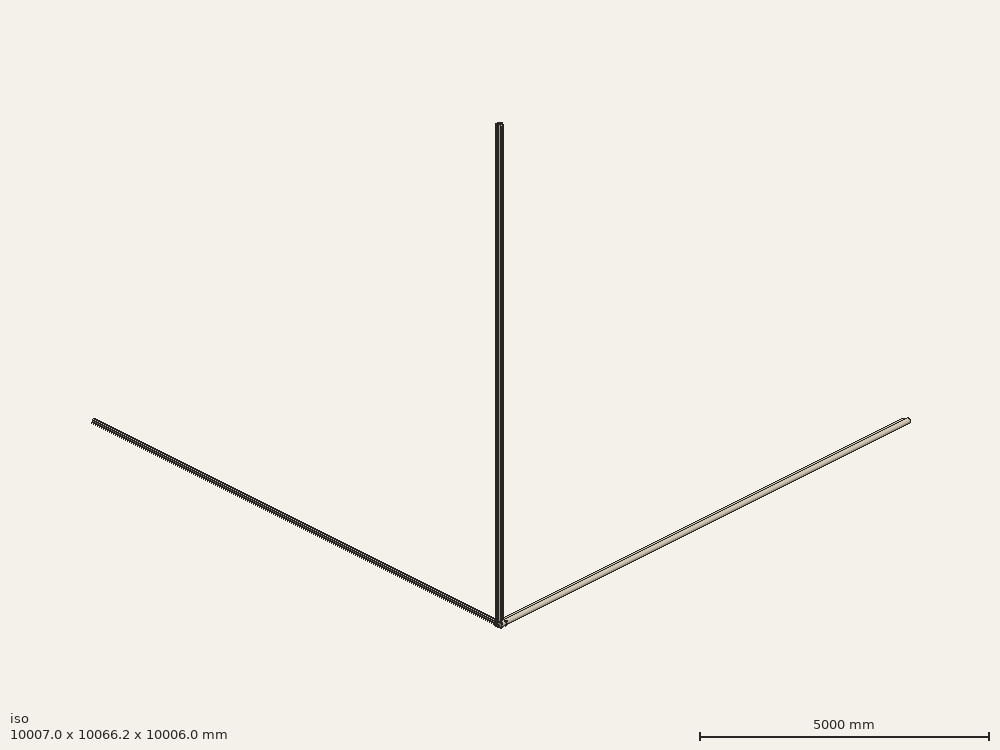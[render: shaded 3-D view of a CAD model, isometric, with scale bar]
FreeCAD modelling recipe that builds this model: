
FCSTD DOCUMENT  (FreeCAD 0.16R6705 (Git))
Label: Hip3
License: All rights reserved
LicenseURL: http://en.wikipedia.org/wiki/All_rights_reserved
objects: PartDesign::Fillet×48, PartDesign::Chamfer×22, Sketcher::SketchObject×16, PartDesign::Pocket×15, PartDesign::PolarPattern×3, PartDesign::Pad×1
note: 121 computed .brp shape members not serialized (recipe doc carries the construction recipe); baked Part::Feature solids carry a one-line shape summary decoded from their .brp

FEATURE [Sketcher::SketchObject] Sketch
  sketch-geometry (29):
    g0: Circle [constr] CenterX=0 CenterY=0 CenterZ=0 NormalX=0 NormalY=0 NormalZ=1 Radius=40
    g1: LineSegment [constr] StartX=-39 StartY=-40 StartZ=0 EndX=-25 EndY=-40 EndZ=0
    g2: LineSegment [constr] StartX=-25 StartY=-40 StartZ=0 EndX=-25 EndY=-120 EndZ=0
    g3: LineSegment [constr] StartX=-25 StartY=-120 StartZ=0 EndX=-39 EndY=-120 EndZ=0
    g4: LineSegment [constr] StartX=-39 StartY=-120 StartZ=0 EndX=-39 EndY=-30 EndZ=0
    g5: LineSegment [constr] StartX=25 StartY=-40 StartZ=0 EndX=39 EndY=-40 EndZ=0
    g6: LineSegment [constr] StartX=39 StartY=-40 StartZ=0 EndX=39 EndY=-120 EndZ=0
    g7: LineSegment [constr] StartX=39 StartY=-120 StartZ=0 EndX=25 EndY=-120 EndZ=0
    g8: LineSegment [constr] StartX=25 StartY=-120 StartZ=0 EndX=25 EndY=-40 EndZ=0
    g9: LineSegment [constr] StartX=-25 StartY=-120 StartZ=0 EndX=25 EndY=-120 EndZ=0
    g10: LineSegment [constr] StartX=-39 StartY=-80 StartZ=0 EndX=39 EndY=-80 EndZ=0
    g11: LineSegment [constr] StartX=-39 StartY=65 StartZ=0 EndX=61 EndY=65 EndZ=0
    g12: LineSegment [constr] StartX=39 StartY=-65 StartZ=0 EndX=-39 EndY=-65 EndZ=0
    g13: GeomPoint [constr] X=0 Y=-80 Z=0
    g14: LineSegment StartX=-68 StartY=44 StartZ=0 EndX=68 EndY=44 EndZ=0
    g15: LineSegment StartX=68 StartY=44 StartZ=0 EndX=68 EndY=-65 EndZ=0
    g16: LineSegment StartX=68 StartY=-65 StartZ=0 EndX=-68 EndY=-65 EndZ=0
    g17: LineSegment StartX=-68 StartY=-65 StartZ=0 EndX=-68 EndY=44 EndZ=0
    g18: LineSegment [constr] StartX=-39 StartY=-30 StartZ=0 EndX=-68 EndY=-30 EndZ=0
    g19: LineSegment [constr] StartX=-68 StartY=-30 StartZ=0 EndX=-68 EndY=-130 EndZ=0
    g20: LineSegment [constr] StartX=-68 StartY=-130 StartZ=0 EndX=-39 EndY=-130 EndZ=0
    g21: LineSegment [constr] StartX=-39 StartY=-130 StartZ=0 EndX=-39 EndY=-120 EndZ=0
    g22: Circle CenterX=0 CenterY=0 CenterZ=0 NormalX=0 NormalY=0 NormalZ=1 Radius=18
    g23: Circle [constr] CenterX=0 CenterY=0 CenterZ=0 NormalX=0 NormalY=0 NormalZ=1 Radius=51
    g24: Circle CenterX=-47 CenterY=-50 CenterZ=0 NormalX=0 NormalY=0 NormalZ=1 Radius=1.7
    g25: Circle CenterX=-47 CenterY=-60 CenterZ=0 NormalX=0 NormalY=0 NormalZ=1 Radius=1.7
    g26: Circle CenterX=47 CenterY=-50 CenterZ=0 NormalX=0 NormalY=0 NormalZ=1 Radius=1.7
    g27: Circle CenterX=47 CenterY=-60 CenterZ=0 NormalX=0 NormalY=0 NormalZ=1 Radius=1.7
    g28: LineSegment [constr] StartX=-47 StartY=-50 StartZ=0 EndX=-47 EndY=-60 EndZ=0
  constraints (81):
    c: Radius(g0) = 40
    c: Coincident(g2,g3)
    c: Coincident(g3,g4)
    c: Horizontal(g3)
    c: Vertical(g2)
    c: Vertical(g4)
    c: Coincident(g5,g6)
    c: Coincident(g6,g7)
    c: Coincident(g7,g8)
    c: Horizontal(g7)
    c: Vertical(g6)
    c: Vertical(g8)
    c: Coincident(g9,g2)
    c: Coincident(g9,g7)
    c: Horizontal(g9)
    c: DistanceX(g1,g5) = 50
    c: DistanceY(g6,g5) = 80
    c: DistanceX(g1,g1) = 14
    c: PointOnObject(g10,g4)
    c: Horizontal(g10)
    c: Symmetric(g5,g6,g10)
    c: Horizontal(g11)
    c: Horizontal(g12)
    c: Symmetric(g12,g11,g-1)
    c: DistanceX(g11,g11) = 100
    c: DistanceY(g10,g12) = 15
    c: Symmetric(g3,g5,g13)
    c: DistanceY(g13,g-1) = 80
    c: Coincident(g0,g-1)
    c: Coincident(g14,g15)
    c: Coincident(g15,g16)
    c: Coincident(g16,g17)
    c: Coincident(g17,g14)
    c: Horizontal(g16)
    c: Vertical(g15)
    c: Vertical(g17)
    c: DistanceX(g14,g14) = 136
    c: DistanceX(g16,g12) = 29
    c: PointOnObject(g12,g16)
    c: Horizontal(g18)
    c: Coincident(g18,g19)
    c: Vertical(g19)
    c: Coincident(g19,g20)
    c: Horizontal(g20)
    c: Coincident(g20,g21)
    c: Coincident(g21,g3)
    c: Vertical(g21)
    c: Symmetric(g18,g20,g10)
    c: DistanceY(g19,g18) = 100
    c: DistanceX(g19,g20) = 29
    c: Horizontal(g14)
    c: Symmetric(g14,g14,g-2)
    c: DistanceY(g16,g14) = 109
    c: Coincident(g22,g-1)
    c: Radius(g22) = 18
    c: Horizontal(g5)
    c: Horizontal(g1)
    c: Symmetric(g5,g1,g-2)
    c: Coincident(g4,g18)
    c: PointOnObject(g1,g4)
    c: PointOnObject(g12,g4)
    c: Coincident(g23,g-1)
    c: Radius(g23) = 51
    c: Coincident(g2,g1)
    c: Coincident(g5,g8)
    c: Symmetric(g5,g1,g-2)
    c: DistanceY(g12,g-1) = 65
    c: Symmetric(g12,g12,g-2)
    c: DistanceY(g-1,g14) = 44
    c: DistanceY(g24,g4) = 20
    c: DistanceY(g25,g24) = 10
    c: Symmetric(g24,g26,g-2)
    c: Symmetric(g25,g27,g-2)
    c: Radius(g27) = 1.7
    c: Equal(g27,g26)
    c: Equal(g27,g24)
    c: Equal(g27,g25)
    c: Coincident(g28,g24)
    c: Coincident(g28,g25)
    c: Vertical(g28)
    c: DistanceX(g24,g1) = 8
FEATURE [PartDesign::Pad] Pad
  Length = 44
  Length2 = 100
  Sketch = -> Sketch
  Type = 0
FEATURE [Sketcher::SketchObject] Sketch001  label="SideCut"
  Placement = pos=(-68,0,0) rot=(0.57735,-0.57735,-0.57735;2.0944rad)
  Support = -> Pad [Face4]
  sketch-geometry (29):
    g0: Circle CenterX=80 CenterY=58 CenterZ=0 NormalX=0 NormalY=0 NormalZ=1 Radius=51.2
    g1: LineSegment [constr] StartX=-50 StartY=-14 StartZ=0 EndX=50 EndY=-14 EndZ=0
    g2: LineSegment [constr] StartX=50 StartY=-14 StartZ=0 EndX=50 EndY=-43 EndZ=0
    g3: LineSegment [constr] StartX=50 StartY=-43 StartZ=0 EndX=-50 EndY=-43 EndZ=0
    g4: LineSegment [constr] StartX=-50 StartY=-43 StartZ=0 EndX=-50 EndY=-14 EndZ=0
    g5: LineSegment [constr] StartX=-40 StartY=0 StartZ=0 EndX=40 EndY=0 EndZ=0
    g6: LineSegment [constr] StartX=40 StartY=0 StartZ=0 EndX=40 EndY=-14 EndZ=0
    g7: LineSegment [constr] StartX=40 StartY=-14 StartZ=0 EndX=-40 EndY=-14 EndZ=0
    g8: LineSegment [constr] StartX=-40 StartY=-14 StartZ=0 EndX=-40 EndY=0 EndZ=0
    g9: LineSegment [constr] StartX=30 StartY=108 StartZ=0 EndX=130 EndY=108 EndZ=0
    g10: LineSegment [constr] StartX=130 StartY=108 StartZ=0 EndX=130 EndY=8 EndZ=0
    g11: LineSegment [constr] StartX=130 StartY=8 StartZ=0 EndX=30 EndY=8 EndZ=0
    g12: LineSegment [constr] StartX=30 StartY=8 StartZ=0 EndX=30 EndY=108 EndZ=0
    g13: LineSegment StartX=22 StartY=50 StartZ=0 EndX=22 EndY=44 EndZ=0
    g14: LineSegment StartX=-8 StartY=14 StartZ=0 EndX=-28 EndY=14 EndZ=0
    g15: LineSegment StartX=-28 StartY=20 StartZ=0 EndX=-50 EndY=20 EndZ=0
    g16: LineSegment StartX=-50 StartY=20 StartZ=0 EndX=-50 EndY=50 EndZ=0
    g17: LineSegment StartX=-50 StartY=50 StartZ=0 EndX=22 EndY=50 EndZ=0
    g18: GeomPoint [constr] X=0 Y=14 Z=0
    g19: LineSegment StartX=32.75 StartY=17.25 StartZ=0 EndX=39.25 EndY=17.25 EndZ=0
    g20: LineSegment StartX=39.25 StartY=17.25 StartZ=0 EndX=39.25 EndY=10.75 EndZ=0
    g21: LineSegment StartX=39.25 StartY=10.75 StartZ=0 EndX=32.75 EndY=10.75 EndZ=0
    g22: LineSegment StartX=32.75 StartY=10.75 StartZ=0 EndX=32.75 EndY=17.25 EndZ=0
    g23: GeomPoint [constr] X=36 Y=14 Z=0
    g24: LineSegment StartX=-28 StartY=20 StartZ=0 EndX=-28 EndY=14 EndZ=0
    g25: Circle CenterX=36 CenterY=23 CenterZ=0 NormalX=0 NormalY=0 NormalZ=1 Radius=1.7
    g26: LineSegment [constr] StartX=36 StartY=23 StartZ=0 EndX=36 EndY=14 EndZ=0
    g27: Circle CenterX=-40 CenterY=14 CenterZ=0 NormalX=0 NormalY=0 NormalZ=1 Radius=1.5
    g28: ArcOfCircle CenterX=-8 CenterY=44 CenterZ=0 NormalX=0 NormalY=0 NormalZ=1 Radius=30 StartAngle=4.71239 EndAngle=6.28319
  constraints (82):
    c: DistanceX(g-1,g0) = 80
    c: Radius(g0) = 51.2
    c: DistanceY(g-1,g0) = 58
    c: Coincident(g1,g2)
    c: Coincident(g2,g3)
    c: Coincident(g3,g4)
    c: Coincident(g4,g1)
    c: Horizontal(g1)
    c: Horizontal(g3)
    c: Vertical(g2)
    c: Vertical(g4)
    c: Symmetric(g1,g1,g-2)
    c: DistanceX(g3,g2) = 100
    c: DistanceY(g3,g1) = 29
    c: DistanceY(g1,g-1) = 14
    c: Coincident(g5,g6)
    c: Coincident(g6,g7)
    c: Coincident(g7,g8)
    c: Coincident(g8,g5)
    c: Horizontal(g5)
    c: Horizontal(g7)
    c: Vertical(g6)
    c: Vertical(g8)
    c: Symmetric(g5,g5,g-2)
    c: DistanceY(g7,g5) = 14
    c: PointOnObject(g-1,g5)
    c: DistanceX(g7,g6) = 80
    c: Coincident(g9,g10)
    c: Coincident(g10,g11)
    c: Coincident(g11,g12)
    c: Coincident(g12,g9)
    c: Horizontal(g9)
    c: Horizontal(g11)
    c: Vertical(g10)
    c: Vertical(g12)
    c: Equal(g10,g9)
    c: Symmetric(g11,g9,g0)
    c: DistanceY(g10,g9) = 100
    c: Vertical(g13)
    c: Horizontal(g14)
    c: Horizontal(g15)
    c: Coincident(g15,g16)
    c: Vertical(g16)
    c: Coincident(g16,g17)
    c: Coincident(g17,g13)
    c: Horizontal(g17)
    c: DistanceX(g13,g9) = 8
    c: DistanceY(g-1,g16) = 50
    c: DistanceX(g16,g-1) = 50
    c: PointOnObject(g18,g14)
    c: PointOnObject(g18,g-2)
    c: DistanceY(g-1,g18) = 14
    c: DistanceX(g-1,g11) = 30
    c: Coincident(g19,g20)
    c: Coincident(g20,g21)
    c: Coincident(g21,g22)
    c: Coincident(g22,g19)
    c: Horizontal(g19)
    c: Horizontal(g21)
    c: Vertical(g20)
    c: Vertical(g22)
    c: Equal(g20,g19)
    c: Symmetric(g20,g19,g23)
    c: DistanceY(g11,g23) = 6
    c: DistanceX(g11,g23) = 6
    c: DistanceY(g20,g19) = 6.5
    c: Coincident(g24,g15)
    c: Vertical(g24)
    c: Coincident(g14,g24)
    c: Radius(g25) = 1.7
    c: DistanceY(g23,g25) = 9
    c: DistanceY(g11,g15) = 12
    c: DistanceX(g15,g18) = 28
    c: Coincident(g26,g25)
    c: Coincident(g26,g23)
    c: Vertical(g26)
    c: DistanceX(g27,g18) = 40
    c: Radius(g27) = 1.5
    c: DistanceY(g27,g15) = 6
    c: Tangent(g13,g28) = 1.5708
    c: Tangent(g14,g28) = 1.5708
    c: DistanceY(g14,g13) = 30
FEATURE [PartDesign::Pocket] Pocket
  Length = 5
  Sketch = -> Sketch001
  Type = 1
FEATURE [Sketcher::SketchObject] Sketch002  label="UpCut"
  Placement = pos=(0,-65,0) rot=(1,0,0;1.5708rad)
  Support = -> Pocket [Face6]
  sketch-geometry (30):
    g0: LineSegment StartX=-25 StartY=50 StartZ=0 EndX=25 EndY=50 EndZ=0
    g1: LineSegment StartX=25 StartY=50 StartZ=0 EndX=25 EndY=14 EndZ=0
    g2: LineSegment StartX=25 StartY=14 StartZ=0 EndX=-25 EndY=14 EndZ=0
    g3: LineSegment StartX=-25 StartY=14 StartZ=0 EndX=-25 EndY=50 EndZ=0
    g4: LineSegment StartX=-65.25 StartY=17.25 StartZ=0 EndX=-58.75 EndY=17.25 EndZ=0
    g5: LineSegment StartX=-58.75 StartY=17.25 StartZ=0 EndX=-58.75 EndY=10.75 EndZ=0
    g6: LineSegment StartX=-58.75 StartY=10.75 StartZ=0 EndX=-65.25 EndY=10.75 EndZ=0
    g7: LineSegment StartX=-65.25 StartY=10.75 StartZ=0 EndX=-65.25 EndY=17.25 EndZ=0
    g8: LineSegment StartX=58.75 StartY=17.25 StartZ=0 EndX=65.25 EndY=17.25 EndZ=0
    g9: LineSegment StartX=65.25 StartY=17.25 StartZ=0 EndX=65.25 EndY=10.75 EndZ=0
    g10: LineSegment StartX=65.25 StartY=10.75 StartZ=0 EndX=58.75 EndY=10.75 EndZ=0
    g11: LineSegment StartX=58.75 StartY=10.75 StartZ=0 EndX=58.75 EndY=17.25 EndZ=0
    g12: GeomPoint [constr] X=62 Y=14 Z=0
    g13: GeomPoint [constr] X=-62 Y=14 Z=0
    g14: Circle CenterX=-47 CenterY=38 CenterZ=0 NormalX=0 NormalY=0 NormalZ=1 Radius=1.7
    g15: Circle CenterX=-47 CenterY=28 CenterZ=0 NormalX=0 NormalY=0 NormalZ=1 Radius=1.7
    g16: Circle CenterX=47 CenterY=38 CenterZ=0 NormalX=0 NormalY=0 NormalZ=1 Radius=1.7
    g17: Circle CenterX=47 CenterY=28 CenterZ=0 NormalX=0 NormalY=0 NormalZ=1 Radius=1.7
    g18: LineSegment [constr] StartX=-68 StartY=108 StartZ=0 EndX=-39 EndY=108 EndZ=0
    g19: LineSegment [constr] StartX=-39 StartY=108 StartZ=0 EndX=-39 EndY=8 EndZ=0
    g20: LineSegment [constr] StartX=-39 StartY=8 StartZ=0 EndX=-68 EndY=8 EndZ=0
    g21: LineSegment [constr] StartX=-68 StartY=8 StartZ=0 EndX=-68 EndY=108 EndZ=0
    g22: LineSegment [constr] StartX=39 StartY=108 StartZ=0 EndX=68 EndY=108 EndZ=0
    g23: LineSegment [constr] StartX=68 StartY=108 StartZ=0 EndX=68 EndY=8 EndZ=0
    g24: LineSegment [constr] StartX=68 StartY=8 StartZ=0 EndX=39 EndY=8 EndZ=0
    g25: LineSegment [constr] StartX=39 StartY=8 StartZ=0 EndX=39 EndY=108 EndZ=0
    g26: LineSegment [constr] StartX=-47 StartY=38 StartZ=0 EndX=-47 EndY=28 EndZ=0
    g27: LineSegment [constr] StartX=47 StartY=38 StartZ=0 EndX=47 EndY=28 EndZ=0
    g28: LineSegment [constr] StartX=-68 StartY=58 StartZ=0 EndX=-39 EndY=58 EndZ=0
    g29: LineSegment [constr] StartX=-39 StartY=8 StartZ=0 EndX=39 EndY=8 EndZ=0
  constraints (87):
    c: Coincident(g0,g1)
    c: Coincident(g3,g0)
    c: Horizontal(g0)
    c: Horizontal(g2)
    c: Vertical(g1)
    c: Vertical(g3)
    c: Symmetric(g0,g0,g-2)
    c: Symmetric(g2,g2,g-2)
    c: DistanceY(g-1,g2) = 14
    c: DistanceY(g-1,g0) = 50
    c: DistanceX(g0,g0) = 50
    c: Coincident(g4,g5)
    c: Coincident(g5,g6)
    c: Coincident(g6,g7)
    c: Coincident(g7,g4)
    c: Horizontal(g4)
    c: Horizontal(g6)
    c: Vertical(g5)
    c: Vertical(g7)
    c: Coincident(g8,g9)
    c: Coincident(g9,g10)
    c: Coincident(g10,g11)
    c: Coincident(g11,g8)
    c: Horizontal(g8)
    c: Horizontal(g10)
    c: Vertical(g9)
    c: Vertical(g11)
    c: Equal(g9,g8)
    c: Equal(g8,g4)
    c: Equal(g4,g7)
    c: DistanceY(g9,g8) = 6.5
    c: Symmetric(g6,g4,g13)
    c: Symmetric(g8,g10,g12)
    c: Symmetric(g12,g13,g-2)
    c: DistanceX(g13,g3) = 37
    c: Coincident(g2,g1)
    c: Coincident(g2,g3)
    c: Radius(g15) = 1.7
    c: Equal(g15,g14)
    c: Equal(g15,g16)
    c: Equal(g15,g17)
    c: Coincident(g18,g19)
    c: Coincident(g19,g20)
    c: Coincident(g20,g21)
    c: Coincident(g21,g18)
    c: Horizontal(g18)
    c: Horizontal(g20)
    c: Vertical(g19)
    c: Vertical(g21)
    c: Coincident(g22,g23)
    c: Coincident(g23,g24)
    c: Coincident(g24,g25)
    c: Coincident(g25,g22)
    c: Horizontal(g22)
    c: Horizontal(g24)
    c: Vertical(g23)
    c: Vertical(g25)
    c: DistanceX(g18,g18) = 29
    c: DistanceY(g20,g18) = 100
    c: DistanceX(g19,g2) = 14
    c: DistanceX(g1,g24) = 14
    c: Symmetric(g18,g22,g-2)
    c: Symmetric(g22,g18,g-2)
    c: Coincident(g26,g14)
    c: Coincident(g26,g15)
    c: Coincident(g27,g16)
    c: Coincident(g27,g17)
    c: Vertical(g27)
    c: DistanceY(g26,g26) = 10
    c: DistanceY(g27,g27) = 10
    c: Symmetric(g14,g16,g-2)
    c: Vertical(g26)
    c: DistanceX(g20,g15) = 21
    c: PointOnObject(g28,g21)
    c: Horizontal(g28)
    c: PointOnObject(g28,g19)
    c: Symmetric(g18,g20,g28)
    c: DistanceY(g14,g28) = 20
    c: Coincident(g29,g19)
    c: Coincident(g29,g24)
    c: Horizontal(g29)
    c: DistanceY(g20,g13) = 6
    c: DistanceY(g19,g15) = 20
    c: DistanceX(g15,g19) = 8
    c: DistanceX(g14,g16) = 94
    c: DistanceY(g-1,g14) = 38
    c: DistanceY(g-1,g20) = 8
FEATURE [PartDesign::Pocket] Pocket001
  Length = 5
  Sketch = -> Sketch002
  Type = 1
FEATURE [Sketcher::SketchObject] Sketch003  label="FixedRingCutout1"
  Placement = pos=(-68,0,0) rot=(0.57735,-0.57735,-0.57735;2.0944rad)
  Support = -> Pocket001 [Face9]
  sketch-geometry (4):
    g0: LineSegment StartX=30 StartY=108 StartZ=0 EndX=130 EndY=108 EndZ=0
    g1: LineSegment StartX=130 StartY=108 StartZ=0 EndX=130 EndY=8 EndZ=0
    g2: LineSegment StartX=130 StartY=8 StartZ=0 EndX=30 EndY=8 EndZ=0
    g3: LineSegment StartX=30 StartY=8 StartZ=0 EndX=30 EndY=108 EndZ=0
  constraints (12):
    c: Coincident(g0,g1)
    c: Coincident(g1,g2)
    c: Coincident(g2,g3)
    c: Coincident(g3,g0)
    c: Horizontal(g0)
    c: Horizontal(g2)
    c: Vertical(g1)
    c: Vertical(g3)
    c: DistanceY(g-1,g2) = 8
    c: DistanceX(g-1,g2) = 30
    c: DistanceY(g1,g0) = 100
    c: DistanceX(g2,g1) = 100
FEATURE [PartDesign::Pocket] Pocket002
  Length = 29
  Sketch = -> Sketch003
  Type = 0
FEATURE [Sketcher::SketchObject] Sketch004  label="FixedRingCutout2"
  Placement = pos=(68,0,0) rot=(0.57735,0.57735,0.57735;2.0944rad)
  Support = -> Pocket002 [Face3]
  sketch-geometry (4):
    g0: LineSegment StartX=-130 StartY=108 StartZ=0 EndX=-30 EndY=108 EndZ=0
    g1: LineSegment StartX=-30 StartY=108 StartZ=0 EndX=-30 EndY=8 EndZ=0
    g2: LineSegment StartX=-30 StartY=8 StartZ=0 EndX=-130 EndY=8 EndZ=0
    g3: LineSegment StartX=-130 StartY=8 StartZ=0 EndX=-130 EndY=108 EndZ=0
  constraints (12):
    c: Coincident(g0,g1)
    c: Coincident(g1,g2)
    c: Coincident(g2,g3)
    c: Coincident(g3,g0)
    c: Horizontal(g0)
    c: Horizontal(g2)
    c: Vertical(g1)
    c: Vertical(g3)
    c: Equal(g0,g3)
    c: DistanceY(g2,g0) = 100
    c: DistanceY(g-1,g1) = 8
    c: DistanceX(g1,g-1) = 30
FEATURE [PartDesign::Pocket] Pocket003
  Length = 29
  Sketch = -> Sketch004
  Type = 0
FEATURE [Sketcher::SketchObject] Sketch007  label="InnerRing"
  Placement = pos=(0,0,14) rot=(0,0,1;0rad)
  Support = -> Pocket003 [Face31]
  sketch-geometry (1):
    g0: Circle CenterX=0 CenterY=0 CenterZ=0 NormalX=0 NormalY=0 NormalZ=1 Radius=29
  constraints (2):
    c: Coincident(g0,g-1)
    c: Radius(g0) = 29
FEATURE [PartDesign::Pocket] Pocket006
  Length = 8
  Sketch = -> Sketch007
  Type = 0
FEATURE [Sketcher::SketchObject] Sketch015  label="InnerRing001"
  Placement = pos=(0,0,6) rot=(0,0,1;0rad)
  Support = -> Pocket006 [Face45]
  sketch-geometry (1):
    g0: Circle CenterX=0 CenterY=0 CenterZ=0 NormalX=0 NormalY=0 NormalZ=1 Radius=29
  constraints (2):
    c: Coincident(g0,g-1)
    c: Radius(g0) = 29
FEATURE [PartDesign::Pocket] Pocket014
  Length = 5
  Reversed = true
  Sketch = -> Sketch015
  Type = 1
FEATURE [Sketcher::SketchObject] Sketch005  label="InnerScrewHole"
  Placement = pos=(0,0,6) rot=(0,0,1;0rad)
  Support = -> Pocket014 [Face45]
  sketch-geometry (1):
    g0: Circle CenterX=0 CenterY=25 CenterZ=0 NormalX=0 NormalY=0 NormalZ=1 Radius=1.7
  constraints (3):
    c: PointOnObject(g0,g-2)
    c: Radius(g0) = 1.7
    c: DistanceY(g-1,g0) = 25
FEATURE [PartDesign::Pocket] Pocket004
  Length = 5
  Sketch = -> Sketch005
  Type = 1
FEATURE [PartDesign::PolarPattern] PolarPattern
  Angle = 360
  Axis = -> Sketch005 [N_Axis]
  Occurrences = 6
  Originals = -> [Pocket004]
FEATURE [Sketcher::SketchObject] Sketch006  label="OuterScrewHole"
  Placement = pos=(0,0,14) rot=(0,0,1;0rad)
  Support = -> PolarPattern [Face37]
  sketch-geometry (1):
    g0: Circle CenterX=34 CenterY=0 CenterZ=0 NormalX=0 NormalY=0 NormalZ=1 Radius=1.7
  constraints (3):
    c: PointOnObject(g0,g-1)
    c: Radius(g0) = 1.7
    c: DistanceX(g-1,g0) = 34
FEATURE [PartDesign::Pocket] Pocket005
  Length = 5
  Sketch = -> Sketch006
  Type = 1
FEATURE [PartDesign::PolarPattern] PolarPattern001
  Angle = 360
  Axis = -> Sketch006 [N_Axis]
  Occurrences = 6
  Originals = -> [Pocket005]
FEATURE [Sketcher::SketchObject] Sketch008  label="CutOuts"
  Placement = pos=(0,0,0) rot=(1,0,0;3.14159rad)
  Support = -> PolarPattern001 [Face2]
  sketch-geometry (24):
    g0: ArcOfCircle CenterX=-65 CenterY=-16 CenterZ=0 NormalX=0 NormalY=0 NormalZ=1 Radius=10 StartAngle=3.14159 EndAngle=6.28319
    g1: ArcOfCircle CenterX=-65 CenterY=10 CenterZ=0 NormalX=0 NormalY=0 NormalZ=1 Radius=10 StartAngle=0 EndAngle=3.14159
    g2: LineSegment StartX=-55 StartY=-16 StartZ=0 EndX=-55 EndY=10 EndZ=0
    g3: LineSegment StartX=-75 StartY=-16 StartZ=0 EndX=-75 EndY=10 EndZ=0
    g4: ArcOfCircle CenterX=65 CenterY=10 CenterZ=0 NormalX=0 NormalY=0 NormalZ=1 Radius=10 StartAngle=0 EndAngle=3.14159
    g5: ArcOfCircle CenterX=65 CenterY=-16 CenterZ=0 NormalX=0 NormalY=0 NormalZ=1 Radius=10 StartAngle=3.14159 EndAngle=6.28319
    g6: LineSegment StartX=55 StartY=10 StartZ=0 EndX=55 EndY=-16 EndZ=0
    g7: LineSegment StartX=75 StartY=10 StartZ=0 EndX=75 EndY=-16 EndZ=0
    g8: ArcOfCircle CenterX=-12 CenterY=60 CenterZ=0 NormalX=0 NormalY=0 NormalZ=1 Radius=18 StartAngle=1.5708 EndAngle=4.71239
    g9: ArcOfCircle CenterX=12 CenterY=60 CenterZ=0 NormalX=0 NormalY=0 NormalZ=1 Radius=18 StartAngle=4.71239 EndAngle=7.85398
    g10: LineSegment StartX=-12 StartY=42 StartZ=0 EndX=12 EndY=42 EndZ=0
    g11: LineSegment StartX=-12 StartY=78 StartZ=0 EndX=12 EndY=78 EndZ=0
    g12: LineSegment [constr] StartX=-65 StartY=20 StartZ=0 EndX=-65 EndY=-26 EndZ=0
    g13: LineSegment [constr] StartX=-30 StartY=60 StartZ=0 EndX=30 EndY=60 EndZ=0
    g14: ArcOfCircle CenterX=-35 CenterY=-44 CenterZ=0 NormalX=0 NormalY=0 NormalZ=1 Radius=9 StartAngle=1.5708 EndAngle=4.71239
    g15: ArcOfCircle CenterX=35 CenterY=-44 CenterZ=0 NormalX=0 NormalY=0 NormalZ=1 Radius=9 StartAngle=4.71239 EndAngle=7.85398
    g16: LineSegment StartX=-35 StartY=-53 StartZ=0 EndX=35 EndY=-53 EndZ=0
    g17: LineSegment StartX=-35 StartY=-35 StartZ=0 EndX=35 EndY=-35 EndZ=0
    g18: Circle CenterX=-35 CenterY=-20 CenterZ=0 NormalX=0 NormalY=0 NormalZ=1 Radius=10
    g19: Circle CenterX=35 CenterY=-20 CenterZ=0 NormalX=0 NormalY=0 NormalZ=1 Radius=10
    g20: Circle CenterX=43 CenterY=8 CenterZ=0 NormalX=0 NormalY=0 NormalZ=1 Radius=7
    g21: Circle CenterX=-43 CenterY=8 CenterZ=0 NormalX=0 NormalY=0 NormalZ=1 Radius=7
    g22: LineSegment [constr] StartX=-43 StartY=8 StartZ=0 EndX=43 EndY=8 EndZ=0
    g23: LineSegment [constr] StartX=38.4638 StartY=-20 StartZ=0 EndX=-35 EndY=-20 EndZ=0
  constraints (62):
    c: Tangent(g0,g3) = 1.5708
    c: Tangent(g0,g2) = -1.5708
    c: Tangent(g2,g1) = -1.5708
    c: Tangent(g3,g1) = 1.5708
    c: Vertical(g2)
    c: Equal(g0,g1)
    c: Tangent(g4,g7) = 1.5708
    c: Tangent(g4,g6) = -1.5708
    c: Tangent(g6,g5) = -1.5708
    c: Tangent(g7,g5) = 1.5708
    c: Equal(g4,g5)
    c: Tangent(g8,g11) = 1.5708
    c: Tangent(g8,g10) = -1.5708
    c: Tangent(g10,g9) = -1.5708
    c: Tangent(g11,g9) = 1.5708
    c: Horizontal(g10)
    c: Equal(g8,g9)
    c: DistanceX(g0,g5) = 130
    c: Symmetric(g0,g5,g-2)
    c: Symmetric(g1,g4,g-2)
    c: Symmetric(g4,g1,g-2)
    c: PointOnObject(g12,g0)
    c: Vertical(g12)
    c: PointOnObject(g12,g1)
    c: PointOnObject(g1,g12)
    c: DistanceY(g12,g-1) = 26
    c: DistanceY(g-1,g12) = 20
    c: DistanceX(g12,g0) = 10
    c: PointOnObject(g13,g8)
    c: PointOnObject(g13,g9)
    c: Horizontal(g13)
    c: PointOnObject(g8,g13)
    c: DistanceX(g13,g13) = 60
    c: Symmetric(g13,g13,g-2)
    c: DistanceY(g9,g9) = 18
    c: Tangent(g14,g17) = 1.5708
    c: Tangent(g14,g16) = -1.5708
    c: Tangent(g16,g15) = -1.5708
    c: Tangent(g17,g15) = 1.5708
    c: Horizontal(g16)
    c: Equal(g14,g15)
    c: DistanceY(g-1,g13) = 60
    c: DistanceY(g14,g-1) = 44
    c: DistanceY(g15,g15) = 9
    c: Horizontal(g22)
    c: Horizontal(g23)
    c: Coincident(g22,g21)
    c: Coincident(g18,g23)
    c: Coincident(g22,g20)
    c: Symmetric(g18,g19,g-2)
    c: Radius(g21) = 7
    c: Equal(g21,g20)
    c: Radius(g18) = 10
    c: Equal(g18,g19)
    c: DistanceY(g-1,g21) = 8
    c: DistanceY(g18,g-1) = 20
    c: DistanceX(g18,g-1) = 35
    c: Symmetric(g14,g15,g-2)
    c: DistanceX(g14,g15) = 70
    c: Symmetric(g21,g20,g-2)
    c: DistanceX(g21,g20) = 86
    c: DistanceY(g-1,g9) = 42
FEATURE [PartDesign::Pocket] Pocket007
  Length = 5
  Sketch = -> Sketch008
  Type = 1
FEATURE [Sketcher::SketchObject] Sketch009  label="BackPocket"
  Placement = pos=(0,44,0) rot=(0,0.707107,0.707107;3.14159rad)
  Support = -> Pocket007 [Face1]
  sketch-geometry (4):
    g0: LineSegment StartX=-45 StartY=28 StartZ=0 EndX=45 EndY=28 EndZ=0
    g1: LineSegment StartX=45 StartY=28 StartZ=0 EndX=45 EndY=8 EndZ=0
    g2: LineSegment StartX=45 StartY=8 StartZ=0 EndX=-45 EndY=8 EndZ=0
    g3: LineSegment StartX=-45 StartY=8 StartZ=0 EndX=-45 EndY=28 EndZ=0
  constraints (12):
    c: Coincident(g0,g1)
    c: Coincident(g1,g2)
    c: Coincident(g2,g3)
    c: Coincident(g3,g0)
    c: Horizontal(g0)
    c: Horizontal(g2)
    c: Vertical(g1)
    c: Vertical(g3)
    c: Symmetric(g2,g1,g-2)
    c: DistanceX(g2,g1) = 90
    c: DistanceY(g-1,g2) = 8
    c: DistanceY(g2,g0) = 20
FEATURE [PartDesign::Pocket] Pocket008
  Length = 23
  Sketch = -> Sketch009
  Type = 0
FEATURE [Sketcher::SketchObject] Sketch010
  Placement = pos=(0,44,0) rot=(0,0.707107,0.707107;3.14159rad)
  Support = -> Pocket008 [Face1]
  sketch-geometry (4):
    g0: LineSegment StartX=-29 StartY=58 StartZ=0 EndX=29 EndY=58 EndZ=0
    g1: LineSegment StartX=29 StartY=58 StartZ=0 EndX=29 EndY=8 EndZ=0
    g2: LineSegment StartX=29 StartY=8 StartZ=0 EndX=-29 EndY=8 EndZ=0
    g3: LineSegment StartX=-29 StartY=8 StartZ=0 EndX=-29 EndY=58 EndZ=0
  constraints (12):
    c: Coincident(g0,g1)
    c: Coincident(g1,g2)
    c: Coincident(g2,g3)
    c: Coincident(g3,g0)
    c: Horizontal(g0)
    c: Horizontal(g2)
    c: Vertical(g1)
    c: Vertical(g3)
    c: Symmetric(g1,g2,g-2)
    c: DistanceY(g-1,g2) = 8
    c: DistanceY(g2,g0) = 50
    c: DistanceX(g0,g0) = 58
FEATURE [PartDesign::Pocket] Pocket009
  Length = 32
  Sketch = -> Sketch010
  Type = 0
FEATURE [Sketcher::SketchObject] Sketch011  label="SideCut001"
  Placement = pos=(-68,0,0) rot=(0.57735,-0.57735,-0.57735;2.0944rad)
  Support = -> Pocket009 [Face24]
  sketch-geometry (4):
    g0: LineSegment StartX=-28 StartY=50 StartZ=0 EndX=22 EndY=50 EndZ=0
    g1: LineSegment StartX=22 StartY=50 StartZ=0 EndX=22 EndY=10 EndZ=0
    g2: LineSegment StartX=22 StartY=10 StartZ=0 EndX=-28 EndY=10 EndZ=0
    g3: LineSegment StartX=-28 StartY=10 StartZ=0 EndX=-28 EndY=50 EndZ=0
  constraints (12):
    c: Coincident(g0,g1)
    c: Coincident(g1,g2)
    c: Coincident(g2,g3)
    c: Coincident(g3,g0)
    c: Horizontal(g0)
    c: Horizontal(g2)
    c: Vertical(g1)
    c: Vertical(g3)
    c: DistanceX(g-1,g1) = 22
    c: DistanceX(g2,g-1) = 28
    c: DistanceY(g-1,g2) = 10
    c: DistanceY(g2,g0) = 40
FEATURE [PartDesign::Pocket] Pocket010
  Length = 10
  Sketch = -> Sketch011
  Type = 0
FEATURE [Sketcher::SketchObject] Sketch012
  Placement = pos=(68,0,0) rot=(0.57735,0.57735,0.57735;2.0944rad)
  Support = -> Pocket010 [Face19]
  sketch-geometry (4):
    g0: LineSegment StartX=-22 StartY=50 StartZ=0 EndX=28 EndY=50 EndZ=0
    g1: LineSegment StartX=28 StartY=50 StartZ=0 EndX=28 EndY=10 EndZ=0
    g2: LineSegment StartX=28 StartY=10 StartZ=0 EndX=-22 EndY=10 EndZ=0
    g3: LineSegment StartX=-22 StartY=10 StartZ=0 EndX=-22 EndY=50 EndZ=0
  constraints (12):
    c: Coincident(g0,g1)
    c: Coincident(g1,g2)
    c: Coincident(g2,g3)
    c: Coincident(g3,g0)
    c: Horizontal(g0)
    c: Horizontal(g2)
    c: Vertical(g1)
    c: Vertical(g3)
    c: DistanceX(g-1,g1) = 28
    c: DistanceX(g2,g-1) = 22
    c: DistanceY(g-1,g2) = 10
    c: DistanceY(g2,g0) = 40
FEATURE [PartDesign::Pocket] Pocket011
  Length = 10
  Sketch = -> Sketch012
  Type = 0
FEATURE [Sketcher::SketchObject] Sketch013  label="OuterScrewHoleAccess"
  Placement = pos=(0,0,8) rot=(0,0,1;0rad)
  Support = -> Pocket011 [Face4]
  sketch-geometry (1):
    g0: Circle CenterX=34 CenterY=0 CenterZ=0 NormalX=0 NormalY=0 NormalZ=1 Radius=3.5
  constraints (3):
    c: PointOnObject(g0,g-1)
    c: Radius(g0) = 3.5
    c: DistanceX(g-1,g0) = 34
FEATURE [PartDesign::Pocket] Pocket012
  Length = 5
  Reversed = true
  Sketch = -> Sketch013
  Type = 1
FEATURE [PartDesign::PolarPattern] PolarPattern002
  Angle = 360
  Axis = -> Sketch013 [N_Axis]
  Occurrences = 6
  Originals = -> [Pocket012]
FEATURE [Sketcher::SketchObject] Sketch014
  Placement = pos=(0,-22,0) rot=(0,0.707107,0.707107;3.14159rad)
  Support = -> PolarPattern002 [Face86]
  sketch-geometry (5):
    g0: Circle CenterX=-47 CenterY=38 CenterZ=0 NormalX=0 NormalY=0 NormalZ=1 Radius=3.5
    g1: Circle CenterX=-47 CenterY=28 CenterZ=0 NormalX=0 NormalY=0 NormalZ=1 Radius=3.5
    g2: Circle CenterX=47 CenterY=38 CenterZ=0 NormalX=0 NormalY=0 NormalZ=1 Radius=3.5
    g3: Circle CenterX=47 CenterY=28 CenterZ=0 NormalX=0 NormalY=0 NormalZ=1 Radius=3.5
    g4: LineSegment [constr] StartX=-47 StartY=38 StartZ=0 EndX=-47 EndY=28 EndZ=0
  constraints (12):
    c: DistanceX(g0,g2) = 94
    c: DistanceY(g-1,g0) = 38
    c: Coincident(g4,g1)
    c: Vertical(g4)
    c: DistanceY(g1,g0) = 10
    c: Symmetric(g1,g3,g-2)
    c: Symmetric(g0,g2,g-2)
    c: Radius(g1) = 3.5
    c: Equal(g1,g0)
    c: Equal(g1,g2)
    c: Equal(g1,g3)
    c: Coincident(g4,g0)
FEATURE [PartDesign::Pocket] Pocket013
  Length = 5
  Reversed = true
  Sketch = -> Sketch014
  Type = 1
FEATURE [PartDesign::Fillet] Fillet
  Base = -> Pocket013 [Edge81]
  Radius = 2
FEATURE [PartDesign::Fillet] Fillet001
  Base = -> Fillet [Edge170]
  Radius = 2
FEATURE [PartDesign::Fillet] Fillet002
  Base = -> Fillet001 [Edge181]
  Radius = 2
FEATURE [PartDesign::Fillet] Fillet003
  Base = -> Fillet002 [Edge163]
  Radius = 2
FEATURE [PartDesign::Fillet] Fillet004
  Base = -> Fillet003 [Edge124]
  Radius = 4
FEATURE [PartDesign::Fillet] Fillet005
  Base = -> Fillet004 [Edge59]
  Radius = 4
FEATURE [PartDesign::Fillet] Fillet006
  Base = -> Fillet005 [Edge132]
  Radius = 4
FEATURE [PartDesign::Fillet] Fillet007
  Base = -> Fillet006 [Edge75]
  Radius = 4
FEATURE [PartDesign::Fillet] Fillet008
  Base = -> Fillet007 [Edge80]
  Radius = 16
FEATURE [PartDesign::Fillet] Fillet009
  Base = -> Fillet008 [Edge90]
  Radius = 16
FEATURE [PartDesign::Fillet] Fillet010
  Base = -> Fillet009 [Edge137]
  Radius = 2
FEATURE [PartDesign::Fillet] Fillet011
  Base = -> Fillet010 [Edge86]
  Radius = 2
FEATURE [PartDesign::Fillet] Fillet012
  Base = -> Fillet011 [Edge224]
  Radius = 3
FEATURE [PartDesign::Fillet] Fillet013
  Base = -> Fillet012 [Edge179]
  Radius = 3
FEATURE [PartDesign::Fillet] Fillet014
  Base = -> Fillet013 [Edge176]
  Radius = 2
FEATURE [PartDesign::Fillet] Fillet015
  Base = -> Fillet014 [Edge73]
  Radius = 2
FEATURE [PartDesign::Fillet] Fillet016
  Base = -> Fillet015 [Edge205]
  Radius = 4
FEATURE [PartDesign::Fillet] Fillet017
  Base = -> Fillet016 [Edge54]
  Radius = 4
FEATURE [PartDesign::Fillet] Fillet018
  Base = -> Fillet017 [Edge181]
  Radius = 6
FEATURE [PartDesign::Fillet] Fillet019
  Base = -> Fillet018 [Edge144]
  Radius = 6
FEATURE [PartDesign::Fillet] Fillet020
  Base = -> Fillet019 [Edge475]
  Radius = 2
FEATURE [PartDesign::Fillet] Fillet021
  Base = -> Fillet020 [Edge20]
  Radius = 2
FEATURE [PartDesign::Fillet] Fillet022
  Base = -> Fillet021 [Edge98]
  Radius = 1
FEATURE [PartDesign::Fillet] Fillet023
  Base = -> Fillet022 [Edge198]
  Radius = 1
FEATURE [PartDesign::Fillet] Fillet024
  Base = -> Fillet023 [Edge101]
  Radius = 1
FEATURE [PartDesign::Fillet] Fillet025
  Base = -> Fillet024 [Edge38]
  Radius = 2
FEATURE [PartDesign::Fillet] Fillet026
  Base = -> Fillet025 [Edge28]
  Radius = 2
FEATURE [PartDesign::Fillet] Fillet027
  Base = -> Fillet026 [Edge61]
  Radius = 2
FEATURE [PartDesign::Fillet] Fillet028
  Base = -> Fillet027 [Edge220]
  Radius = 2
FEATURE [PartDesign::Fillet] Fillet029
  Base = -> Fillet028 [Edge72]
  Radius = 1
FEATURE [PartDesign::Fillet] Fillet030
  Base = -> Fillet029 [Edge4]
  Radius = 1
FEATURE [PartDesign::Fillet] Fillet031
  Base = -> Fillet030 [Edge7]
  Radius = 1
FEATURE [PartDesign::Fillet] Fillet032
  Base = -> Fillet031 [Edge389]
  Radius = 1
FEATURE [PartDesign::Fillet] Fillet033
  Base = -> Fillet032 [Edge261]
  Radius = 0.5
FEATURE [PartDesign::Fillet] Fillet034
  Base = -> Fillet033 [Edge252]
  Radius = 0.5
FEATURE [PartDesign::Fillet] Fillet035
  Base = -> Fillet034 [Edge127]
  Radius = 1
FEATURE [PartDesign::Fillet] Fillet036
  Base = -> Fillet035 [Edge270]
  Radius = 1
FEATURE [PartDesign::Fillet] Fillet037
  Base = -> Fillet036 [Edge235]
  Radius = 1
FEATURE [PartDesign::Fillet] Fillet038
  Base = -> Fillet037 [Edge391]
  Radius = 2
FEATURE [PartDesign::Fillet] Fillet039
  Base = -> Fillet038 [Edge173]
  Radius = 2
FEATURE [PartDesign::Fillet] Fillet040
  Base = -> Fillet039 [Edge79]
  Radius = 3
FEATURE [PartDesign::Fillet] Fillet041
  Base = -> Fillet040 [Edge77]
  Radius = 3
FEATURE [PartDesign::Chamfer] Chamfer
  Base = -> Fillet041 [Edge207]
  Size = 1.5
FEATURE [PartDesign::Chamfer] Chamfer001
  Base = -> Chamfer [Edge179]
  Size = 1.5
FEATURE [PartDesign::Chamfer] Chamfer002
  Base = -> Chamfer001 [Edge177]
  Size = 1.5
FEATURE [PartDesign::Chamfer] Chamfer003
  Base = -> Chamfer002 [Edge61]
  Size = 1.5
FEATURE [PartDesign::Chamfer] Chamfer004
  Base = -> Chamfer003 [Edge7]
  Size = 1.5
FEATURE [PartDesign::Chamfer] Chamfer005
  Base = -> Chamfer004 [Edge7]
  Size = 1.5
FEATURE [PartDesign::Chamfer] Chamfer006
  Base = -> Chamfer005 [Edge6]
  Size = 1.5
FEATURE [PartDesign::Chamfer] Chamfer007
  Base = -> Chamfer006 [Edge8]
  Size = 1.5
FEATURE [PartDesign::Chamfer] Chamfer008
  Base = -> Chamfer007 [Edge248]
  Size = 1.5
FEATURE [PartDesign::Chamfer] Chamfer009
  Base = -> Chamfer008 [Edge29]
  Size = 1.5
FEATURE [PartDesign::Chamfer] Chamfer010
  Base = -> Chamfer009 [Edge357]
  Size = 1.5
FEATURE [PartDesign::Chamfer] Chamfer011
  Base = -> Chamfer010 [Edge198]
  Size = 1.5
FEATURE [PartDesign::Chamfer] Chamfer012
  Base = -> Chamfer011 [Edge558]
  Size = 1.5
FEATURE [PartDesign::Chamfer] Chamfer013
  Base = -> Chamfer012 [Edge49]
  Size = 1.5
FEATURE [PartDesign::Chamfer] Chamfer014
  Base = -> Chamfer013 [Edge687]
  Size = 1.5
FEATURE [PartDesign::Chamfer] Chamfer015
  Base = -> Chamfer014 [Edge49]
  Size = 1.5
FEATURE [PartDesign::Chamfer] Chamfer016
  Base = -> Chamfer015 [Edge103]
  Size = 1.5
FEATURE [PartDesign::Chamfer] Chamfer017
  Base = -> Chamfer016 [Edge49]
  Size = 1.5
FEATURE [PartDesign::Chamfer] Chamfer018
  Base = -> Chamfer017 [Edge50]
  Size = 1.5
FEATURE [PartDesign::Chamfer] Chamfer019
  Base = -> Chamfer018 [Edge36]
  Size = 1.5
FEATURE [PartDesign::Chamfer] Chamfer020
  Base = -> Chamfer019 [Edge606]
  Size = 1.5
FEATURE [PartDesign::Chamfer] Chamfer021
  Base = -> Chamfer020 [Edge485]
  Size = 1.5
FEATURE [PartDesign::Fillet] Fillet042
  Base = -> Chamfer021 [Edge183]
  Radius = 1
FEATURE [PartDesign::Fillet] Fillet043
  Base = -> Fillet042 [Edge483]
  Radius = 1
FEATURE [PartDesign::Fillet] Fillet044
  Base = -> Fillet043 [Edge483]
  Radius = 0.5
FEATURE [PartDesign::Fillet] Fillet045
  Base = -> Fillet044 [Edge613]
  Radius = 0.1
FEATURE [PartDesign::Fillet] Fillet046
  Base = -> Fillet045 [Edge54]
  Radius = 0.1
FEATURE [PartDesign::Fillet] Fillet047
  Base = -> Fillet046 [Edge10]
  Radius = 0.1
